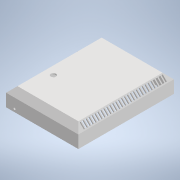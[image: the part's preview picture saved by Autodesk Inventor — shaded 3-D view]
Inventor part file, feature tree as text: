
AUTODESK INVENTOR PART (.ipt)
format: ipt  version: 2020.2 (Build 242310000, 310)  size: 446,464 bytes
history: native  units: in
note: dims shown in document units (in); Inventor stores cm internally (conversion verified against a paired STEP export)
features: sketch x9, hole x8, other x7, reference x4, fillet x2, extrude x1
ambient origin geometry x8: Origin, YZ Plane, XZ Plane, XY Plane, X Axis, Y Axis, Z Axis, Center Point
bodies: Solid1 (feature_tree)
feature tree (31):
  other  "Back_Case.ipt"
  extrude  "Extrusion1"  Depth=0.25in
  hole  "Hole1"  [1 undecoded]
  hole  "Hole2"  [1 undecoded]
  hole  "Hole3"  [1 undecoded]
  hole  "Hole4"  [1 undecoded]
  hole  "Hole7"  [1 undecoded]
  hole  "Hole8"  [1 undecoded]
  hole  "Hole9"  [1 undecoded]
  fillet  "Fillet1"  Radius=0.735in
  fillet  "Fillet2"  Radius=0.25in
  hole  "Hole10"  [1 undecoded]
  other  "Vented Case::Back_Case.ipt"
  other  "TaggingFeature1"
  sketch  "Sketch1"  dims[d0=0.3937in d1=0.25in]
  reference  "Reference1"
  reference  "Reference2"
  reference  "Reference3"
  reference  "Reference4"
  sketch  "Sketch2"  dims[d2=0.25in d3=0.25in]
  sketch  "Sketch3"  dims[d4=0.25in d5=0.25in d6=0.0in]
  sketch  "Sketch4"  dims[d7=0.0968in d8=0.2in d9=0.375in d10=0.25in d11=0.5635in d12=0.2in d13=0.0in]
  sketch  "Sketch5"  dims[d14=0.0968in d15=0.2in d16=0.375in d17=0.25in d18=0.5635in d19=0.2in d20=0.0in]
  sketch  "Sketch8"  dims[d21=0.0968in d22=0.2in d23=0.375in d24=0.25in d25=0.5635in d26=0.2in d27=0.0in]
  sketch  "Sketch9"  dims[d28=0.0968in d29=0.2in d30=0.375in d31=0.25in d32=0.5635in d33=0.2in d34=0.0in d53=0.25in]
  sketch  "Sketch10"  dims[d54=2.0in]
  sketch  "Sketch11"  dims[d55=0.177in d56=0.315in d57=0.37in d58=0.25in d59=90.0deg d60=0.465in d61=0.0in d62=2.0in d63=0.25in d64=0.177in d65=0.315in d66=0.37in d67=0.25in d68=90.0deg d69=0.465in d70=0.0in d71=0.42in d72=0.315in d73=0.37in d74=0.25in d75=90.0deg d76=0.465in d77=0.0in d78=0.0312in d79=0.0625in d80=0.735in d81=0.25in d82=0.177in d83=0.315in d84=0.37in d85=0.25in d86=90.0deg d87=0.465in d88=0.0in]
  parser-record x1  (decoder bookkeeping rows leaked as tree rows — omitted from the tree; the rows remain in map.json)
  other  "Back_Case.iam"
  other  "raspberrypi_3_stripped:1"
  other  "Raspberry Pi 31:1"
note: 8 required parameter values undecoded (feature->parameter linkage not recoverable at this tier; creation-order binding heuristic only, values carry confidence <= 0.55)
note: 1 file-system path scrubbed to <path> (originals preserved in map.json)
